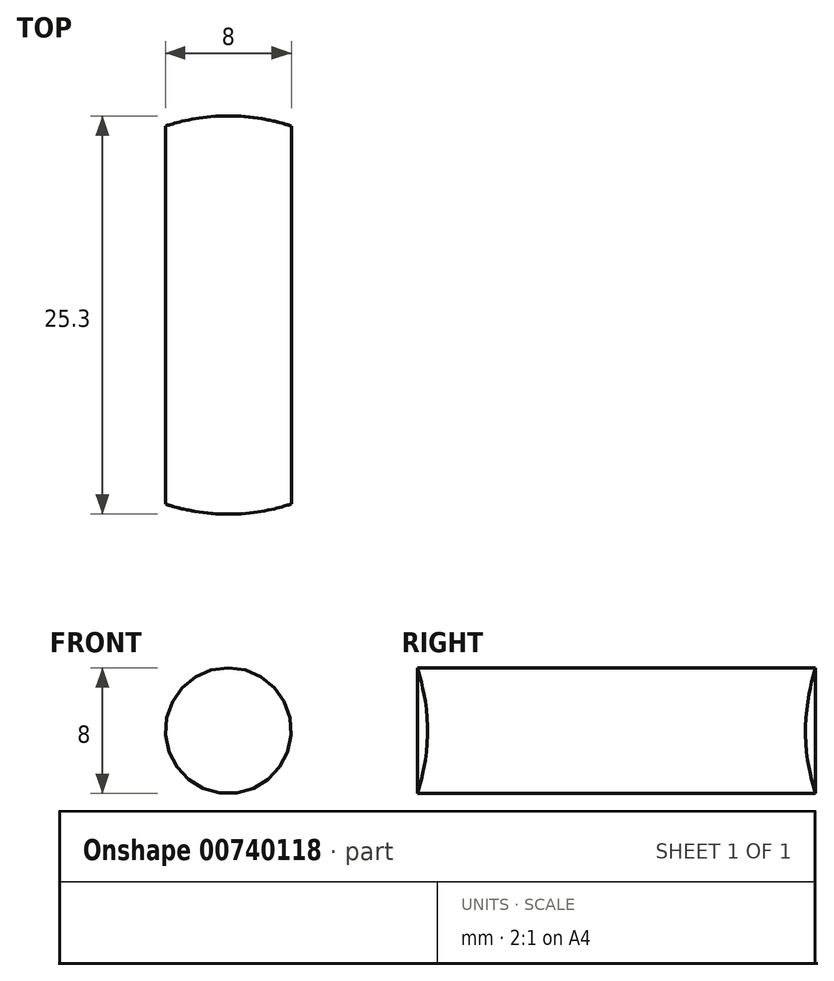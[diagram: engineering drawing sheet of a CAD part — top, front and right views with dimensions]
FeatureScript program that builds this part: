
annotation { "Feature Type Name" : "Feature", "Feature Type Description" : "" }
export const myFeature = defineFeature(function(context is Context, id is Id, definition is map)
    precondition{}
    {
        {
            var Q0;
            Q0=qCreatedBy(makeId("Front.planeOp"),FACE);
            var sketch = newSketch(context, id + "F0", { "sketchPlane" : qUnion([Q0])});
            skCircle(sketch, "E0", {"center": v(0, 0) * mm, "radius": 4 * mm});
            skSolve(sketch);
        }
        {
            var Q0;
            Q0=makeQuery(id+"F0.imprint","IMPRINT",FACE,{"disambiguationData":[TD([[makeQuery(id+"F0.imprint","IMPRINT",EDGE,{"derivedFrom":sQuery(id+"F0.wireOp",EDGE,"E0")}),1.0]])]});
            extrude(context, id + "F1", {"entities" : qUnion([Q0]), "depth" : 92.8 * mm, "offsetDistance" : 25 * mm, "symmetric" : true});
        }
        {
            var Q0;
            Q0=qCreatedBy(makeId("Top.planeOp"),FACE);
            var sketch = newSketch(context, id + "F2", { "sketchPlane" : qUnion([Q0])});
            skCircle(sketch, "E1", {"center": v(0, 0) * mm, "radius": 12.65 * mm});
            skCircle(sketch, "E2", {"center": v(0, 0) * mm, "radius": 49.75 * mm});
            skSolve(sketch);
        }
        {
            var Q0;
            Q0 = qSketchRegion(id + "F2", true);
            extrude(context, id + "F3", {"entities" : qUnion([Q0]), "operationType" : NewBodyOperationType.REMOVE, "oppositeDirection" : true, "depth" : 51.2 * mm, "offsetDistance" : 25 * mm, "symmetric" : true});
        }
    });
